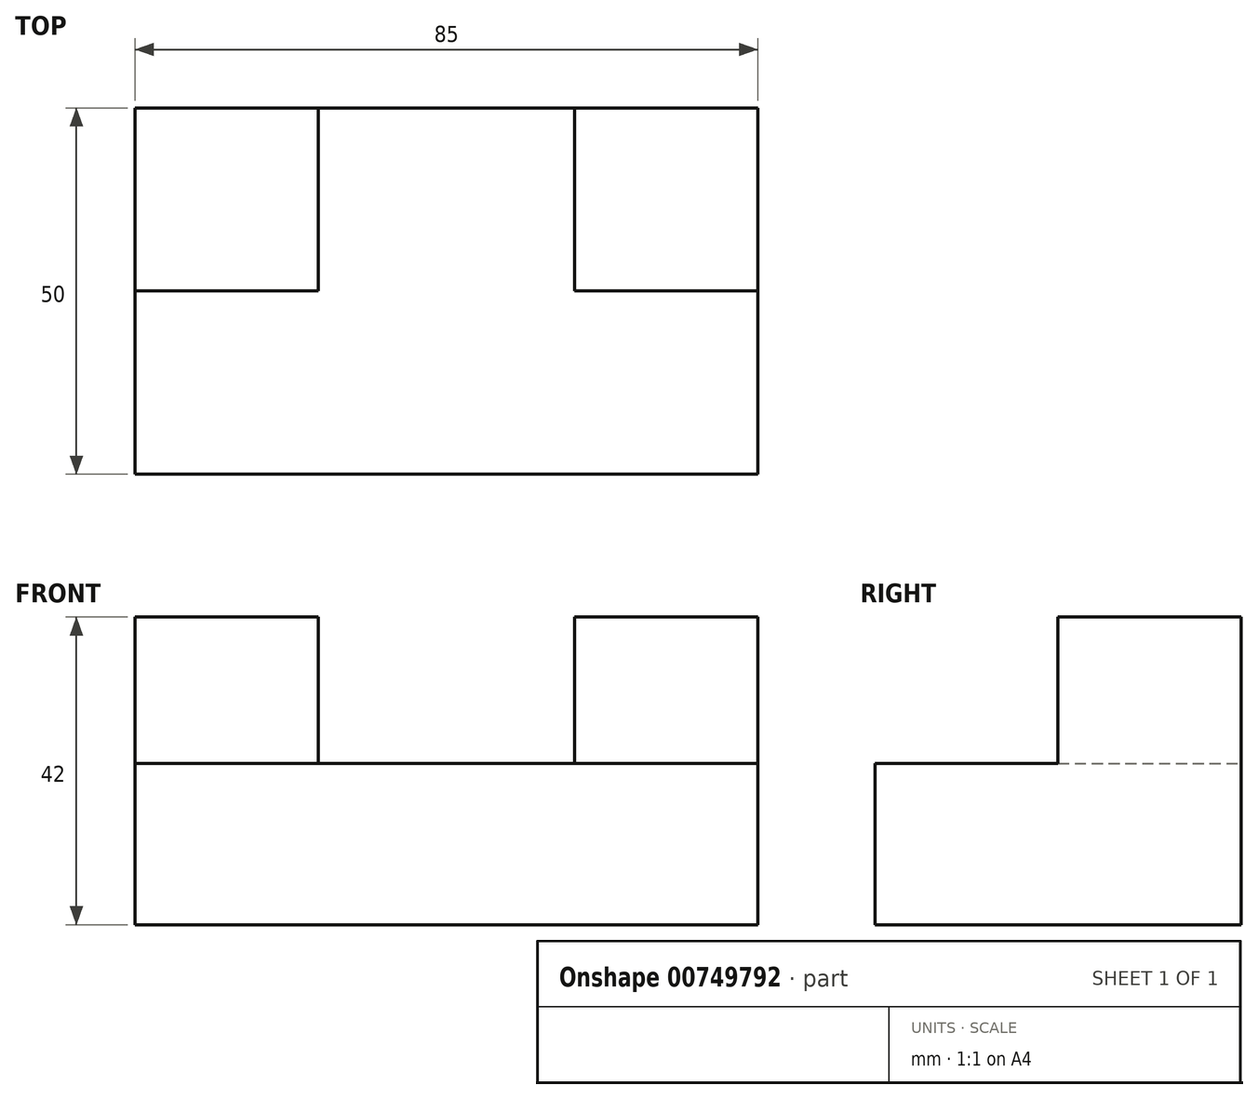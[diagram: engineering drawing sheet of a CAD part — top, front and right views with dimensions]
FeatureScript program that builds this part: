
annotation { "Feature Type Name" : "Feature", "Feature Type Description" : "" }
export const myFeature = defineFeature(function(context is Context, id is Id, definition is map)
    precondition{}
    {
        {
            var Q0;
            Q0=qCreatedBy(makeId("Front.planeOp"),FACE);
            var sketch = newSketch(context, id + "F0", { "sketchPlane" : qUnion([Q0])});
            skLineSegment(sketch, "E0.bottom", {"start": v(0, 0) * mm, "end": v(85, 0) * mm});
            skLineSegment(sketch, "E0.top", {"start": v(0, -22) * mm, "end": v(85, -22) * mm});
            skLineSegment(sketch, "E0.left", {"start": v(0, 0) * mm, "end": v(0, -22) * mm});
            skLineSegment(sketch, "E0.right", {"start": v(85, 0) * mm, "end": v(85, -22) * mm});
            skLineSegment(sketch, "E1.bottom", {"start": v(0, 0) * mm, "end": v(25, 0) * mm});
            skLineSegment(sketch, "E1.top", {"start": v(0, 20) * mm, "end": v(25, 20) * mm});
            skLineSegment(sketch, "E1.left", {"start": v(0, 0) * mm, "end": v(0, 20) * mm});
            skLineSegment(sketch, "E1.right", {"start": v(25, 0) * mm, "end": v(25, 20) * mm});
            skLineSegment(sketch, "E2.bottom", {"start": v(85, 0) * mm, "end": v(60, 0) * mm});
            skLineSegment(sketch, "E2.top", {"start": v(85, 20) * mm, "end": v(60, 20) * mm});
            skLineSegment(sketch, "E2.left", {"start": v(85, 0) * mm, "end": v(85, 20) * mm});
            skLineSegment(sketch, "E2.right", {"start": v(60, 0) * mm, "end": v(60, 20) * mm});
            skSolve(sketch);
        }
        {
            var Q0;
            Q0=makeQuery(id+"F0.imprint","IMPRINT",FACE,{"disambiguationData":[TD([[makeQuery(id+"F0.imprint","IMPRINT",EDGE,{"derivedFrom":sQuery(id+"F0.wireOp",EDGE,"E0.bottom")}),-1.0]])]});
            extrude(context, id + "F1", {"entities" : qUnion([Q0]), "depth" : 50 * mm, "offsetDistance" : 25 * mm});
        }
        {
            var Q0;
            Q0 = qSketchRegion(id + "F0", true);
            extrude(context, id + "F2", {"entities" : qUnion([Q0]), "operationType" : NewBodyOperationType.ADD, "depth" : 25 * mm, "offsetDistance" : 25 * mm});
        }
    });
